FCSTD DOCUMENT  (FreeCAD 0.19R)
Label: WIng-1
License: All rights reserved
LicenseURL: http://en.wikipedia.org/wiki/All_rights_reserved
objects: Sketcher::SketchObject×2, App::DocumentObjectGroup×1, Part::Part2DObjectPython×1, PartDesign::Body×1, Part::FeaturePython×1
note: 5 computed .brp shape members not serialized (recipe doc carries the construction recipe); baked Part::Feature solids carry a one-line shape summary decoded from their .brp

FEATURE [App::DocumentObjectGroup] ag03
FEATURE [Part::Part2DObjectPython] Wire  # Draft 2D object (typed FeaturePython)
  Area = 0.0416322
  ChamferSize = 0
  Closed = true
  End = (1,0,-0.000548)
  FilletRadius = 0
  Length = 2.01856
  MakeFace = true
  Placement = pos=(0,0,0) rot=(1,0,0;1.5708rad)
  Points = (180) [(1,0.000662,0),(0.994875,0.00121,0),(0.984975,0.002247,0),(0.973308,0.003426,0),(0.960939,0.004647,0),(0.94837,0.005887,0),(0.935754,0.00714,0),+173 more]
  Start = (1,0,0.000662)
  Subdivisions = 10
FEATURE [Sketcher::SketchObject] Sketch
  MapMode = 5
  Support = -> [XY_Plane]
  sketch-geometry (12):
    g0: Circle [constr] CenterX=-18.4034 CenterY=0 CenterZ=0 NormalX=0 NormalY=0 NormalZ=1 AngleXU=0 Radius=6
    g1: Circle [constr] CenterX=-14.5355 CenterY=33.8363 CenterZ=0 NormalX=0 NormalY=0 NormalZ=1 AngleXU=0 Radius=6
    g2: Circle [constr] CenterX=-7.87319 CenterY=58.4222 CenterZ=0 NormalX=0 NormalY=0 NormalZ=1 AngleXU=0 Radius=6
    g3: BSplineCurve PolesCount=3 KnotsCount=2 Degree=2 IsPeriodic=0
    g4: GeomPoint [constr] X=-18.4034 Y=0 Z=0
    g5: GeomPoint [constr] X=-7.87319 Y=58.4222 Z=0
    g6: Circle [constr] CenterX=28.263 CenterY=0 CenterZ=0 NormalX=0 NormalY=0 NormalZ=1 AngleXU=0 Radius=5
    g7: Circle [constr] CenterX=27.038 CenterY=30.5545 CenterZ=0 NormalX=0 NormalY=0 NormalZ=1 AngleXU=0 Radius=5
    g8: Circle [constr] CenterX=21.7151 CenterY=59.4885 CenterZ=0 NormalX=0 NormalY=0 NormalZ=1 AngleXU=0 Radius=5
    g9: BSplineCurve PolesCount=3 KnotsCount=2 Degree=2 IsPeriodic=0
    g10: GeomPoint [constr] X=28.263 Y=0 Z=0
    g11: GeomPoint [constr] X=21.7151 Y=59.4885 Z=0
  constraints (18):
    c: PointOnObject(g3,g-1)
    c: Radius(g0) = 6
    c: Equal(g0,g1)
    c: Equal(g0,g2)
    c: InternalAlignment(g0,g3)
    c: InternalAlignment(g1,g3)
    c: InternalAlignment(g2,g3)
    c: InternalAlignment(g4,g3)
    c: InternalAlignment(g5,g3)
    c: PointOnObject(g9,g-1)
    c: Radius(g6) = 5
    c: Equal(g6,g7)
    c: Equal(g6,g8)
    c: InternalAlignment(g6,g9)
    c: InternalAlignment(g7,g9)
    c: InternalAlignment(g8,g9)
    c: InternalAlignment(g10,g9)
    c: InternalAlignment(g11,g9)
FEATURE [Sketcher::SketchObject] Sketch001
  MapMode = 5
  Placement = pos=(0,0,0) rot=(0.57735,0.57735,0.57735;2.0944rad)
  Support = -> [YZ_Plane]
  sketch-geometry (2):
    g0: LineSegment StartX=0 StartY=13.7247 StartZ=0 EndX=59.1989 EndY=8.92358 EndZ=0
    g1: LineSegment StartX=0 StartY=-11.104 StartZ=0 EndX=59.8848 EndY=-11.104 EndZ=0
  constraints (3):
    c: PointOnObject(g0,g-2)
    c: PointOnObject(g1,g-2)
    c: Horizontal(g1)
FEATURE [PartDesign::Body] Body
  Group = -> [Sketch,Sketch001,Wire]
  Origin = -> Origin
FEATURE [Part::FeaturePython] CurvedArray  # WARN: FeaturePython — macro-defined, semantics opaque (R4)
  Axis = (0,1,0)
  Base = -> Wire
  Distribution = 0
  DistributionReverse = false
  Hullcurves = -> [Sketch,Sketch001]
  Items = 6
  OffsetEnd = 0
  OffsetStart = 0
  Solid = false
  Surface = true
  Twist = 0
